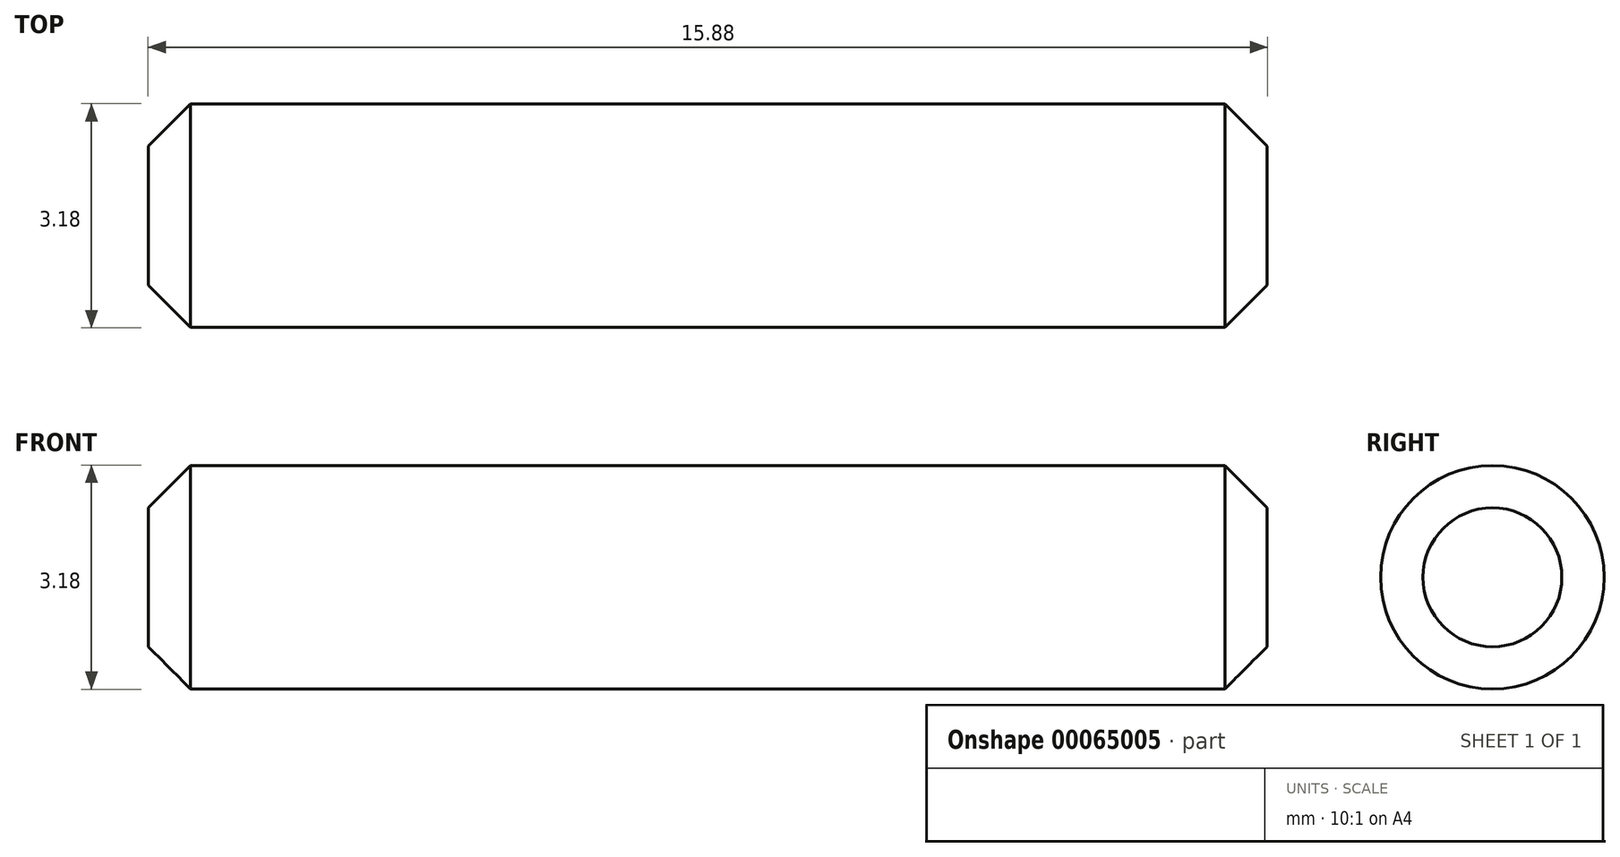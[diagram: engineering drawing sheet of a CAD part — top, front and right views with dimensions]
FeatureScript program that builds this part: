
annotation { "Feature Type Name" : "Feature", "Feature Type Description" : "" }
export const myFeature = defineFeature(function(context is Context, id is Id, definition is map)
    precondition{}
    {
        {
            var Q0;
            Q0=qCreatedBy(makeId("Right.planeOp"),FACE);
            var sketch = newSketch(context, id + "F0", { "sketchPlane" : qUnion([Q0])});
            skCircle(sketch, "E0", {"center": v(0, 0) * mm, "radius": 1.59 * mm});
            skSolve(sketch);
        }
        {
            var Q0;
            Q0 = qSketchRegion(id + "F0", true);
            extrude(context, id + "F1", {"entities" : qUnion([Q0]), "endBound" : BoundingType.SYMMETRIC, "depth" : 15.87 * mm});
        }
        {
            var Q0;
            Q0=makeQuery(id+"F1.opExtrude","SWEPT_FACE",FACE,{"disambiguationData":[OSD([sQuery(id+"F0.wireOp",EDGE,"E0")])]});
            chamfer(context, id + "F2", {"entities" : qUnion([Q0]), "width" : 0.6 * mm, "tangentPropagation" : true});
        }
    });
